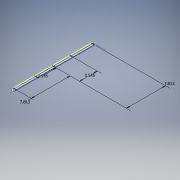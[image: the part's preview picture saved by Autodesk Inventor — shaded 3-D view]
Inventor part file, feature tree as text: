
AUTODESK INVENTOR PART (.ipt)
format: ipt  version: 2017 (Build 210142000, 142)  size: 148,992 bytes
history: native  units: in
note: dims shown in document units (in); Inventor stores cm internally (conversion verified against a paired STEP export)
features: sketch x5, split x1, fillet x1
ambient origin geometry x8: Origin, YZ Plane, XZ Plane, XY Plane, X Axis, Y Axis, Z Axis, Center Point
bodies: Solid1 (feature_tree)
feature tree (7):
  sketch  "Sketch1"  dims[d11=16.0in]
  split  "Split1"
  sketch  "Sketch3"  dims[d13=7.8125in]
  sketch  "Sketch4"  dims[d14=3.5453in]
  sketch  "Sketch5"  dims[d15=3.5453in]
  sketch  "Sketch2"  dims[d12=7.8125in]
  fillet  "Fillet1"  Radius=8.5in
